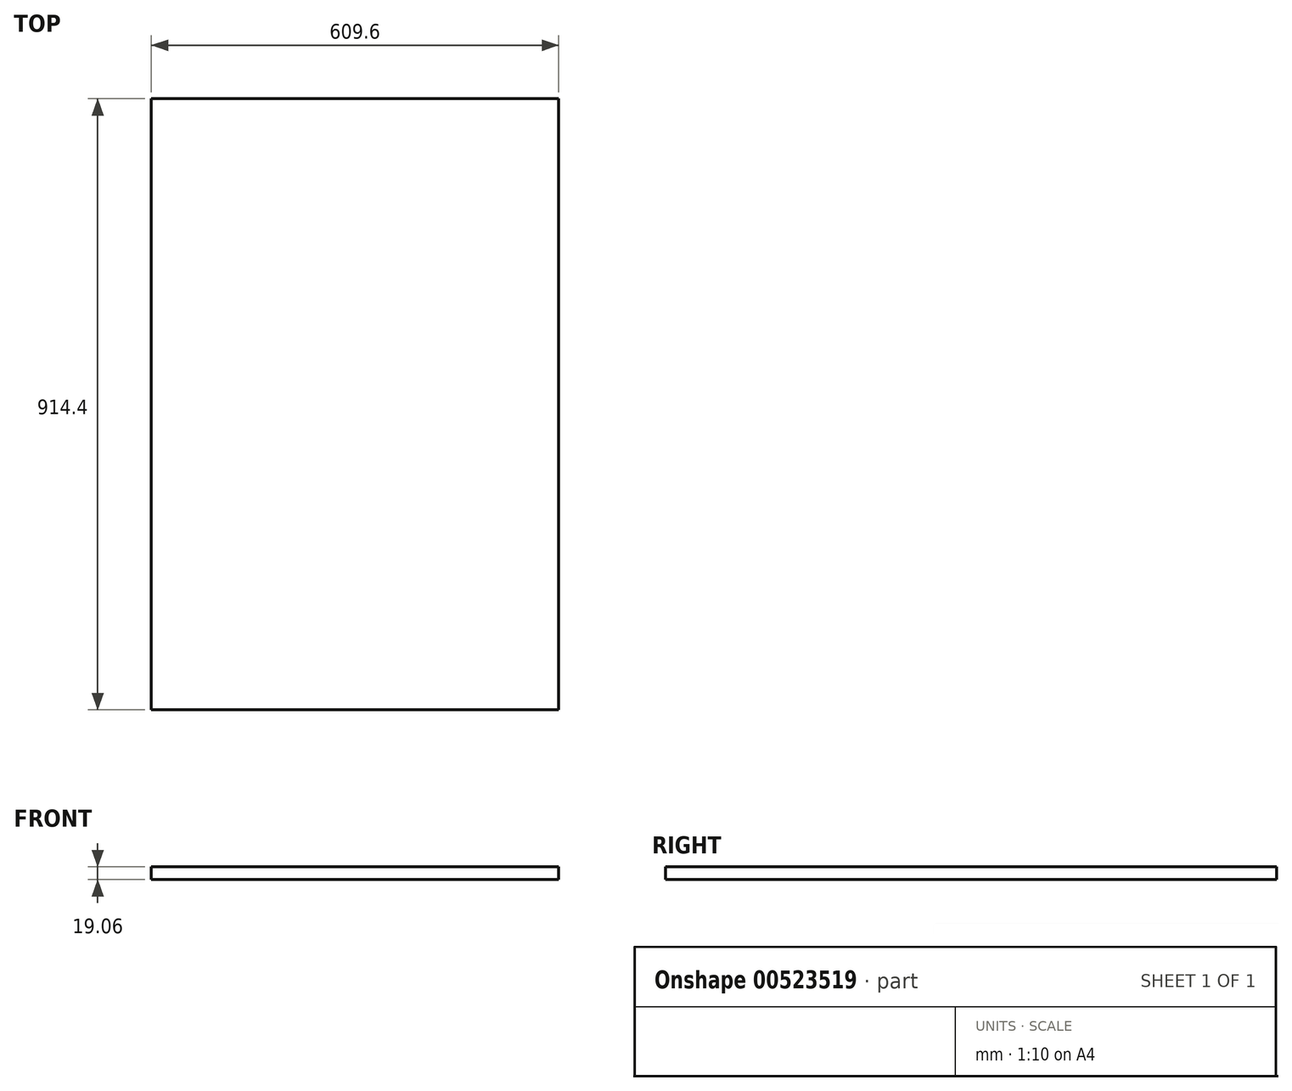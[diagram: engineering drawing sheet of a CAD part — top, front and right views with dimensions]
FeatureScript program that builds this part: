
annotation { "Feature Type Name" : "Feature", "Feature Type Description" : "" }
export const myFeature = defineFeature(function(context is Context, id is Id, definition is map)
    precondition{}
    {
        {
            var Q0;
            Q0=qCreatedBy(makeId("Top.planeOp"),FACE);
            var sketch = newSketch(context, id + "F0", { "sketchPlane" : qUnion([Q0])});
            skLineSegment(sketch, "E0.bottom", {"start": v(-304.8, 457.2) * mm, "end": v(304.8, 457.2) * mm});
            skLineSegment(sketch, "E0.top", {"start": v(-304.8, -457.2) * mm, "end": v(304.8, -457.2) * mm});
            skLineSegment(sketch, "E0.left", {"start": v(-304.8, 457.2) * mm, "end": v(-304.8, -457.2) * mm});
            skLineSegment(sketch, "E0.right", {"start": v(304.8, 457.2) * mm, "end": v(304.8, -457.2) * mm});
            skPoint(sketch, "E0.middle", {"position": v(0, 0) * mm});
            skSolve(sketch);
        }
        {
            var Q0;
            Q0=makeQuery(id+"F0.imprint","IMPRINT",FACE,{"disambiguationData":[TD([[makeQuery(id+"F0.imprint","IMPRINT",EDGE,{"derivedFrom":sQuery(id+"F0.wireOp",EDGE,"E0.bottom")}),-1.0]])]});
            extrude(context, id + "F1", {"entities" : qUnion([Q0]), "endBound" : BoundingType.SYMMETRIC, "depth" : 19.05 * mm, "offsetDistance" : 25.4 * mm});
        }
    });
